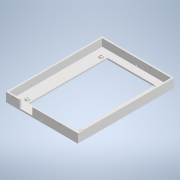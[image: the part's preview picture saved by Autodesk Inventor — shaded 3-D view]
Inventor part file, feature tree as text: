
AUTODESK INVENTOR PART (.ipt)
format: ipt  version: 2020.2 (Build 242310000, 310)  size: 227,840 bytes
history: native  units: in
note: dims shown in document units (in); Inventor stores cm internally (conversion verified against a paired STEP export)
features: sketch x11, hole x10, other x3, extrude x1, fillet x1
ambient origin geometry x8: Origin, YZ Plane, XZ Plane, XY Plane, X Axis, Y Axis, Z Axis, Center Point
bodies: Solid1 (feature_tree)
feature tree (26):
  other  "Back_Case.ipt"
  hole  "Hole3"  [1 undecoded]
  hole  "Hole4"  [1 undecoded]
  hole  "Hole5"  [1 undecoded]
  hole  "Hole6"  [1 undecoded]
  hole  "Hole7"  [1 undecoded]
  hole  "Hole8"  [1 undecoded]
  extrude  "Extrusion2"  Depth=0.625in
  fillet  "Fillet2"  Radius=1.15in
  hole  "Hole9"  [1 undecoded]
  hole  "Hole10"  [1 undecoded]
  hole  "Hole11"  [1 undecoded]
  hole  "Hole12"  [1 undecoded]
  other  "Inner Case::Back_Case.ipt"
  other  "TaggingFeature1"
  sketch  "Sketch3"  dims[d0=0.3937in d15=0.2in]
  sketch  "Sketch4"  dims[d16=3.0in]
  sketch  "Sketch5"  dims[d17=0.1in d18=0.315in d19=0.37in d20=0.25in d21=90.0deg d22=0.465in d23=0.0in d24=0.2in]
  sketch  "Sketch6"  dims[d25=3.0in]
  sketch  "Sketch7"  dims[d26=0.1in d27=0.315in d28=0.37in d29=0.25in d30=90.0deg d31=0.465in d32=0.0in d33=0.2in]
  sketch  "Sketch8"  dims[d34=2.0in]
  sketch  "Sketch10"  dims[d35=0.1in d36=0.315in d37=0.37in d38=0.25in d39=90.0deg d40=0.465in d41=0.0in d42=0.2in]
  sketch  "Sketch11"  dims[d43=2.0in]
  sketch  "Sketch12"  dims[d44=0.1in d45=0.315in d46=0.37in d47=0.25in d48=90.0deg d49=0.465in d50=0.0in d51=0.2in]
  sketch  "Sketch13"  dims[d52=2.0in]
  sketch  "Sketch14"  dims[d53=0.1in d54=0.315in d55=0.37in d56=0.25in d57=90.0deg d58=0.465in d59=0.0in d60=0.2in d61=2.0in d62=0.1in d63=0.315in d64=0.37in d65=0.25in d66=90.0deg d67=0.465in d68=0.0in d74=1.15in d75=1.05in d76=0.125in d77=0.0in d78=0.0612in d79=0.625in d80=1.84in d81=0.1276in d82=0.315in d83=0.375in d84=0.25in d85=0.5635in d86=0.465in d87=0.0in d88=0.625in d89=1.87in d90=0.1276in d91=0.315in d92=0.375in d93=0.25in d94=0.5635in d95=0.465in d96=0.0in d97=0.625in d98=1.5105in d99=0.1276in d100=0.315in d101=0.375in d102=0.25in d103=0.5635in d104=0.465in d105=0.0in d106=0.6in d107=0.625in d108=0.1276in d109=0.315in d110=0.375in d111=0.25in d112=0.5635in d113=0.465in d114=0.0in]
note: 10 required parameter values undecoded (feature->parameter linkage not recoverable at this tier; creation-order binding heuristic only, values carry confidence <= 0.55)
